# Revit family: equip-sink-elkay-double-lustertone
name_source: partatom
category: Generic Models
units: mm (PartAtom-declared; Revit-internal decimal feet)

## family parameters
Always vertical = Yes
Can host rebar = No
Cut with Voids When Loaded = No
Part Type = Normal
Room Calculation Point = No
Round Connector Dimension = Use Diameter
Shared = No
Work Plane-Based = No

## types (4) — shared parameters
2D Hole 1 = Yes
2D Hole 2 = Yes
2D Hole 3 = Yes
2D Hole 4 = Yes
2D Hole 5 = No
Bowl Length = 1' - 2"
CL Sink to CL Partition = 0' - 0"
Custom Bowl = No
Custom Bowl Length = 1' - 2"
Deep Specification Sheet URL = http://www.elkayusa.com
Description = Lustertone Double Bowl Sink
Drain Location = 0' - 8"
Faucet Hole CL = 0' - 2 1/4"
Hole 1 Top = 0' - 2"
Hole 1 from CL = 0' - 4"
Hole 1 to 2 = 0' - 4"
Hole 1 to 3 = 0' - 8"
Hole 1 to 4 = 1' - 0"
Hole 1 to 5 = 1' - 3"
Hole 1 to 6 = 1' - 6"
Hole 1 to 7 = 1' - 9"
Hole 1 to 8 = 2' - 0"
Hole 2 Top = 0' - 2"
Hole 3 Top = 0' - 2"
Hole 4 Top = 0' - 2"
Hole 5 Top = 0' - 1 1/2"
Installation Sheet URL = http://www.elkayusa.com
Left Bowl Length = 1' - 2"
Manufacturer = Elkay Manufacturing
Model = LR3321
Partition Width = 0' - 1 1/4"
Sink Bowl Formula = 1' - 2"
Sink Depth = 0' - 7 5/8"
Sink Ledge Back Width = 0' - 4"
Sink Ledge Front Width = 0' - 1 1/2"
Sink Ledge Sides Width = 0' - 1 7/8"
Sink Length = 2' - 9"
Sink Material = <By Category>
Sink Width = 1' - 9 1/4"
Specification Sheet URL = http://www.elkayusa.com
URL = www.elkayusa.com

## type names (no varying parameters)
- ByType
- LR3321
- LR3319
- DLR332210

## geometry (parser evidence)
native form markers: Sweep x5
no freeform markers — native parametric forms only
